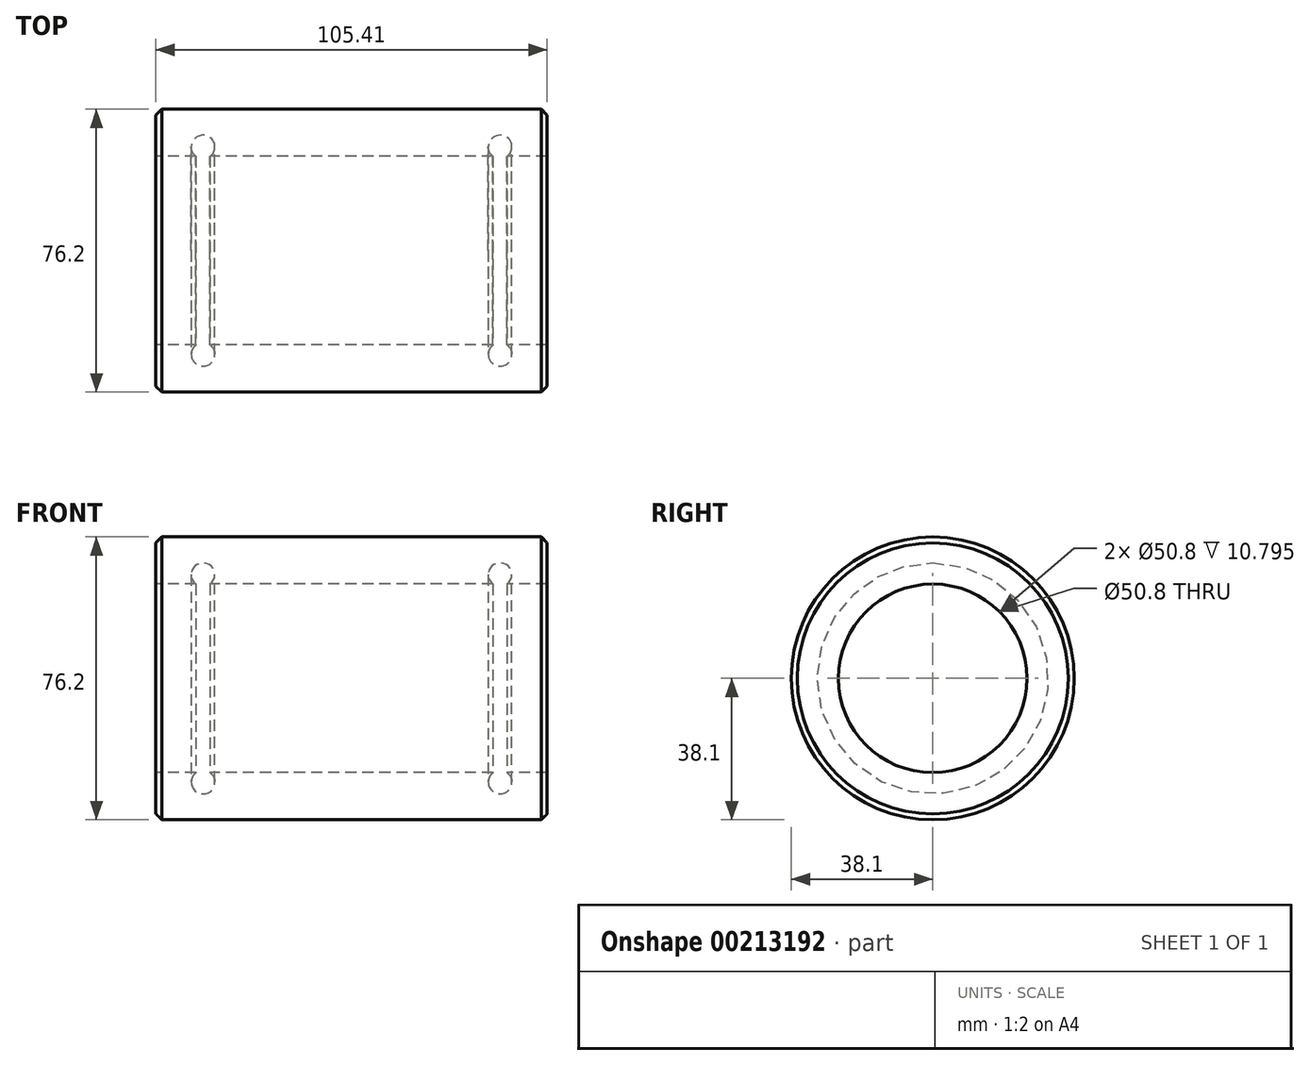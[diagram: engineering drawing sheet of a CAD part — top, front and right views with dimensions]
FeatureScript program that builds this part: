
annotation { "Feature Type Name" : "Feature", "Feature Type Description" : "" }
export const myFeature = defineFeature(function(context is Context, id is Id, definition is map)
    precondition{}
    {
        {
            var Q0;
            Q0=qCreatedBy(makeId("Front.planeOp"),FACE);
            var sketch = newSketch(context, id + "F0", { "sketchPlane" : qUnion([Q0])});
            skLineSegment(sketch, "E0", {"start": v(0, 0) * mm, "end": v(127, 0) * mm, "construction": true});
            skLineSegment(sketch, "E1.bottom", {"start": v(0, 38.1) * mm, "end": v(105.41, 38.1) * mm});
            skLineSegment(sketch, "E1.top", {"start": v(0, 25.4) * mm, "end": v(10.8, 25.4) * mm});
            skLineSegment(sketch, "E1.left", {"start": v(0, 38.1) * mm, "end": v(0, 25.4) * mm});
            skLineSegment(sketch, "E1.right", {"start": v(105.41, 38.1) * mm, "end": v(105.41, 25.4) * mm});
            skArc(sketch, "E2", {"start": v(14.6, 25.4) * mm, "mid": v(12.7, 31.12) * mm, "end": v(10.8, 25.4) * mm});
            skArc(sketch, "E3", {"start": v(94.62, 25.4) * mm, "mid": v(92.71, 31.12) * mm, "end": v(90.8, 25.4) * mm});
            skLineSegment(sketch, "E4.trimOffspring", {"start": v(14.6, 25.4) * mm, "end": v(90.8, 25.4) * mm});
            skLineSegment(sketch, "E5.trimOffspring", {"start": v(94.62, 25.4) * mm, "end": v(105.41, 25.4) * mm});
            skSolve(sketch);
        }
        {
            var Q0;
            Q0=makeQuery(id+"F0.imprint","IMPRINT",FACE,{"disambiguationData":[TD([[makeQuery(id+"F0.imprint","IMPRINT",EDGE,{"derivedFrom":sQuery(id+"F0.wireOp",EDGE,"E1.bottom")}),-1.0]])]});
            var Q1;
            Q1=sQuery(id+"F0.wireOp",EDGE,"E0");
            revolve(context, id + "F1", {"entities" : qUnion([Q0]), "axis" : qUnion([Q1]), "revolveType" : RevolveType.FULL});
        }
        {
            var Q0;
            Q0=makeQuery(id+"F1.opRevolve","SWEPT_EDGE",EDGE,{"disambiguationData":[OSD([sQuery(id+"F0.wireOp",EDGE,"E1.bottom"),sQuery(id+"F0.wireOp",EDGE,"E1.right")])]});
            var Q1;
            Q1=makeQuery(id+"F1.opRevolve","SWEPT_EDGE",EDGE,{"disambiguationData":[OSD([sQuery(id+"F0.wireOp",EDGE,"E1.bottom"),sQuery(id+"F0.wireOp",EDGE,"E1.left")])]});
            chamfer(context, id + "F2", {"entities" : qUnion([Q0, Q1]), "width" : 1.6 * mm, "tangentPropagation" : true});
        }
    });
